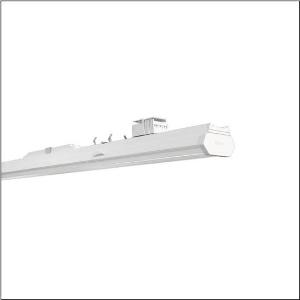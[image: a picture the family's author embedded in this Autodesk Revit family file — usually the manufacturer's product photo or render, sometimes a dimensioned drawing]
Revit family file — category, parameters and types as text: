
# Revit family: licross_r__11_protected_mo_51td1bdn49xg3s4_3b80
name_source: partatom
category: Lighting Fixtures
units: mm (PartAtom-declared; Revit-internal decimal feet)

## family parameters
Cut with Voids When Loaded = No
Host = Face
Light Source = No
Part Type = Normal
Room Calculation Point = No
Round Connector Dimension = Use Diameter
Shared = No

## types (1)
- --- (1 x LED, 920 lm, 6.8 W, 4000K)
    Apparent Load = 7 VA
    CIE Flux Codes = 54 82 95 97 100
    Color Rendering = 80
    Color Temperature = 4000K
    Default Elevation = 1800 mm
    Description = Licross® 11 Protected MO, luminaire insert, of sheet steel, galvanised, coil coated, white, length: 1.500mm, width: 90mm, height: 101mm, LED rated luminous flux: 9.370lm, light colour: 840, SDCM (Standard Deviation of Colour Matching)MacAdam ≤ 2 SDCM (initial), control gear: DALI 2, with plug, 6-pole, with phase selection, for trunking rail, 9 or 11-core, mains connection: 220..240V, AC, 50/60Hz, rated input power: 61W, for trunking rail, 9-/11-core, internal wiring halogen-free, for emergency light function, converter,control gear: single battery element, battery: LiFePO4, 9Ah, primary optical cover: cover, of PMMA, light emission: direct distribution, primary light characteristic: symmetric, protection rating (complete): IP54, insulation class (complete): insulation class I (protective earthing), certification: CE, UKCA, protection symbol: D if used in an environment with non-conductive dust loads with corresponding accessories, impact resistance: IK06, permissible ambient temperature for indoor applications: +5..+35°C, standard: EN 60598-2-22, LABS conformity tested according to VDMA 24364:2018-05, reducing of maximum allowable ambient temperature of 5°C with ceiling mounting, corresponds to IFS (International Featured Standards) requirements for safety and quality in the food industry, packaging unit: 1 piece
    Height = 92 mm
    Lamp = 1 x LED
    Lamp Light Flux = 920 lm
    Lamp Power = 6.8 W
    Lamp count = 1
    Length = 1500 mm
    Luminous efficacy = 135 lm/W
    Manufacturer = Siteco
    ModVariant = No
    Model = 51TD1BDN49XG3S4
    Mounting Place = Ceiling
    Mounting Type = Pendant
    Number of Poles = 1
    OnlyDefault = Yes
    Power Factor = 1
    Product Name = Licross® 11 Protected MO
    Product group = luminaire insert | ceiling pendant
    ProductGroupID = 901
    Protection Class = Protection class I
    Protection Degree = IP 54
    RLX_Detail_Level = 1
    RLX_Emergency_Light_Flux = 0 lm
    RLX_Emergency_Type = 0
    RLX_Emergency_Type_DB = No
    RlxData = <blob elided: 24845 chars, md5=4c3e3c8e>
    Socket = socket
    Standby Power = 0 W
    System Light Flux = 920 lm
    System Power = 7 W
    Type Comments = : emergency light operation: 3 h
    Type Image = l_1256145.jpg
    URL = http://relux.com
    VarID = @adj_098879
    Voltage = 0 V
    Weight = 0.00 kg
    Width = 88 mm

## geometry (parser evidence)
native form markers: Blend x4, Sweep x10
no freeform markers — native parametric forms only
